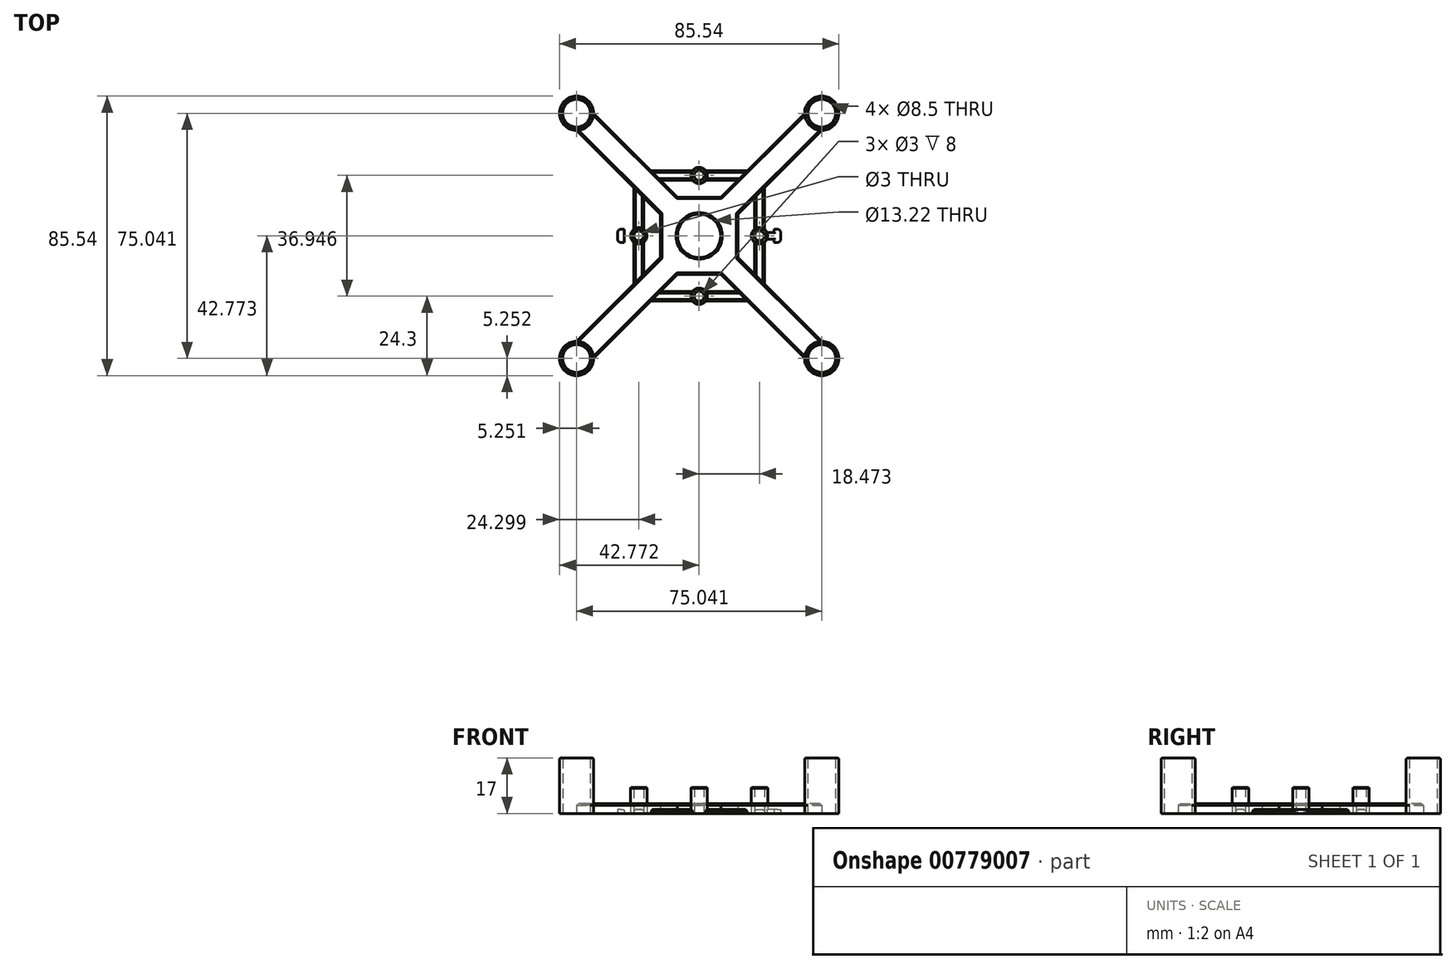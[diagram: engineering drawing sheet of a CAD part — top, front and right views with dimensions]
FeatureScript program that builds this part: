
annotation { "Feature Type Name" : "Feature", "Feature Type Description" : "" }
export const myFeature = defineFeature(function(context is Context, id is Id, definition is map)
    precondition{}
    {
        {
            var Q0;
            Q0=qCreatedBy(makeId("Top.planeOp"),FACE);
            var sketch = newSketch(context, id + "F0", { "sketchPlane" : qUnion([Q0])});
            skCircle(sketch, "E0", {"center": v(-48.89, -12.36) * mm, "radius": 4.25 * mm});
            skCircle(sketch, "E1", {"center": v(26.15, -12.36) * mm, "radius": 4.25 * mm});
            skCircle(sketch, "E2", {"center": v(26.15, 62.68) * mm, "radius": 4.25 * mm});
            skCircle(sketch, "E3", {"center": v(-48.89, 62.68) * mm, "radius": 4.25 * mm});
            skCircle(sketch, "E4", {"center": v(-48.89, 62.68) * mm, "radius": 5.25 * mm});
            skCircle(sketch, "E5", {"center": v(26.15, 62.68) * mm, "radius": 5.25 * mm});
            skCircle(sketch, "E6", {"center": v(26.15, -12.36) * mm, "radius": 5.25 * mm});
            skCircle(sketch, "E7", {"center": v(-48.89, -12.36) * mm, "radius": 5.25 * mm});
            skLineSegment(sketch, "E8", {"start": v(-43.64, -12.36) * mm, "end": v(-17.98, 13.3) * mm});
            skLineSegment(sketch, "E9", {"start": v(-48.89, -7.1) * mm, "end": v(-23.23, 18.55) * mm});
            skLineSegment(sketch, "E10", {"start": v(20.9, -12.36) * mm, "end": v(-4.76, 13.3) * mm});
            skLineSegment(sketch, "E11", {"start": v(26.15, -7.1) * mm, "end": v(0.5, 18.55) * mm});
            skLineSegment(sketch, "E12", {"start": v(20.9, 62.68) * mm, "end": v(-4.76, 37.02) * mm});
            skLineSegment(sketch, "E13", {"start": v(26.15, 57.43) * mm, "end": v(0.5, 31.77) * mm});
            skLineSegment(sketch, "E14", {"start": v(-43.64, 62.68) * mm, "end": v(-17.98, 37.02) * mm});
            skLineSegment(sketch, "E15", {"start": v(-48.89, 57.43) * mm, "end": v(-23.23, 31.77) * mm});
            skCircle(sketch, "E16", {"center": v(7.1, 25.16) * mm, "radius": 1.5 * mm});
            skCircle(sketch, "E17", {"center": v(-11.37, 43.64) * mm, "radius": 1.5 * mm});
            skCircle(sketch, "E18", {"center": v(-29.84, 25.16) * mm, "radius": 1.5 * mm});
            skCircle(sketch, "E19", {"center": v(-11.37, 6.69) * mm, "radius": 1.5 * mm});
            skCircle(sketch, "E20", {"center": v(-29.84, 25.16) * mm, "radius": 2.5 * mm});
            skCircle(sketch, "E21", {"center": v(-11.37, 43.64) * mm, "radius": 2.5 * mm});
            skCircle(sketch, "E22", {"center": v(7.1, 25.16) * mm, "radius": 2.5 * mm});
            skCircle(sketch, "E23", {"center": v(-11.37, 6.69) * mm, "radius": 2.5 * mm});
            skLineSegment(sketch, "E24", {"start": v(-36.34, 25.16) * mm, "end": v(-36.34, 27.16) * mm});
            skLineSegment(sketch, "E25", {"start": v(-36.34, 27.16) * mm, "end": v(-34.34, 27.16) * mm});
            skLineSegment(sketch, "E26", {"start": v(-34.34, 27.16) * mm, "end": v(-34.34, 23.16) * mm});
            skLineSegment(sketch, "E27", {"start": v(-34.34, 23.16) * mm, "end": v(-36.34, 23.16) * mm});
            skLineSegment(sketch, "E28", {"start": v(-36.34, 23.16) * mm, "end": v(-36.34, 25.16) * mm});
            skPoint(sketch, "E29.firstSnap0", {"position": v(-36.34, 26.16) * mm});
            skPoint(sketch, "E29.oppositeSnap0", {"position": v(-36.34, 24.16) * mm});
            skLineSegment(sketch, "E29.left", {"start": v(-34.34, 26.16) * mm, "end": v(-34.34, 24.16) * mm});
            skLineSegment(sketch, "E30", {"start": v(13.6, 25.16) * mm, "end": v(13.6, 27.16) * mm});
            skLineSegment(sketch, "E31", {"start": v(13.6, 27.16) * mm, "end": v(11.6, 27.16) * mm});
            skLineSegment(sketch, "E32", {"start": v(11.6, 27.16) * mm, "end": v(11.6, 23.16) * mm});
            skLineSegment(sketch, "E33", {"start": v(11.6, 23.16) * mm, "end": v(13.6, 23.16) * mm});
            skLineSegment(sketch, "E34", {"start": v(13.6, 23.16) * mm, "end": v(13.6, 25.16) * mm});
            skPoint(sketch, "E35.startSnap0", {"position": v(13.6, 26.16) * mm});
            skLineSegment(sketch, "E36", {"start": v(-34.34, 24.16) * mm, "end": v(-32.13, 24.16) * mm});
            skLineSegment(sketch, "E37", {"start": v(-34.34, 26.16) * mm, "end": v(-32.13, 26.16) * mm});
            skLineSegment(sketch, "E38", {"start": v(11.6, 24.16) * mm, "end": v(9.4, 24.16) * mm});
            skLineSegment(sketch, "E39", {"start": v(11.6, 26.16) * mm, "end": v(9.4, 26.16) * mm});
            skLineSegment(sketch, "E40", {"start": v(-23.23, 31.77) * mm, "end": v(-23.23, 18.55) * mm});
            skLineSegment(sketch, "E41", {"start": v(-17.98, 13.3) * mm, "end": v(-4.76, 13.3) * mm});
            skLineSegment(sketch, "E42", {"start": v(0.5, 18.55) * mm, "end": v(0.5, 31.77) * mm});
            skLineSegment(sketch, "E43", {"start": v(-4.76, 37.02) * mm, "end": v(-17.98, 37.02) * mm});
            skLineSegment(sketch, "E44", {"start": v(-28.34, 25.16) * mm, "end": v(-28.34, 36.89) * mm});
            skLineSegment(sketch, "E45", {"start": v(-28.34, 25.16) * mm, "end": v(-28.34, 13.44) * mm});
            skLineSegment(sketch, "E46", {"start": v(-31.34, 25.16) * mm, "end": v(-31.34, 39.89) * mm});
            skLineSegment(sketch, "E47", {"start": v(-31.34, 25.16) * mm, "end": v(-31.34, 10.44) * mm});
            skLineSegment(sketch, "E48", {"start": v(-11.37, 8.19) * mm, "end": v(-23.1, 8.19) * mm});
            skLineSegment(sketch, "E49", {"start": v(-11.37, 8.19) * mm, "end": v(0.35, 8.19) * mm});
            skLineSegment(sketch, "E50", {"start": v(-11.37, 5.19) * mm, "end": v(3.35, 5.19) * mm});
            skLineSegment(sketch, "E51", {"start": v(-11.37, 5.19) * mm, "end": v(-26.1, 5.19) * mm});
            skLineSegment(sketch, "E52", {"start": v(5.6, 25.16) * mm, "end": v(5.6, 13.44) * mm});
            skLineSegment(sketch, "E53", {"start": v(5.6, 25.16) * mm, "end": v(5.6, 36.89) * mm});
            skLineSegment(sketch, "E54", {"start": v(8.6, 25.16) * mm, "end": v(8.6, 39.89) * mm});
            skLineSegment(sketch, "E55", {"start": v(8.6, 25.16) * mm, "end": v(8.6, 10.44) * mm});
            skLineSegment(sketch, "E56", {"start": v(-11.37, 45.14) * mm, "end": v(3.35, 45.14) * mm});
            skLineSegment(sketch, "E57", {"start": v(-11.37, 45.14) * mm, "end": v(-26.1, 45.14) * mm});
            skLineSegment(sketch, "E58", {"start": v(-11.37, 42.14) * mm, "end": v(0.35, 42.14) * mm});
            skLineSegment(sketch, "E59", {"start": v(-11.37, 42.14) * mm, "end": v(-23.1, 42.14) * mm});
            skCircle(sketch, "E60", {"center": v(-11.37, 25.16) * mm, "radius": 6.61 * mm});
            skSolve(sketch);
        }
        {
            var Q0;
            {var subQ0=sQuery(id+"F0.wireOp",EDGE,"E45");var subQ1=sQuery(id+"F0.wireOp",EDGE,"E9");var subQ2=makeQuery(id+"F0.imprint","INTERSECT",VERTEX,{"derivedFrom":[subQ1,subQ0]});Q0=makeQuery(id+"F0.imprint","IMPRINT",FACE,{"disambiguationData":[TD([[makeQuery(id+"F0.imprint","IMPRINT",EDGE,{"disambiguationData":[TD([[subQ2,1.0]])],"derivedFrom":subQ1}),1.0]])]});}
            var Q1;
            {var subQ0=sQuery(id+"F0.wireOp",EDGE,"E56");var subQ1=sQuery(id+"F0.wireOp",EDGE,"E12");var subQ2=makeQuery(id+"F0.imprint","INTERSECT",VERTEX,{"derivedFrom":[subQ1,subQ0]});Q1=makeQuery(id+"F0.imprint","IMPRINT",FACE,{"disambiguationData":[TD([[makeQuery(id+"F0.imprint","IMPRINT",EDGE,{"disambiguationData":[TD([[subQ2,-1.0]])],"derivedFrom":subQ1}),-1.0]])]});}
            var Q2;
            {var subQ0=sQuery(id+"F0.wireOp",EDGE,"E57");var subQ1=sQuery(id+"F0.wireOp",EDGE,"E14");var subQ2=makeQuery(id+"F0.imprint","INTERSECT",VERTEX,{"derivedFrom":[subQ1,subQ0]});Q2=makeQuery(id+"F0.imprint","IMPRINT",FACE,{"disambiguationData":[TD([[makeQuery(id+"F0.imprint","IMPRINT",EDGE,{"disambiguationData":[TD([[subQ2,-1.0]])],"derivedFrom":subQ1}),1.0]])]});}
            var Q3;
            {var subQ21=sQuery(id+"F0.wireOp",EDGE,"E40");Q3=makeQuery(id+"F0.imprint","IMPRINT",FACE,{"disambiguationData":[TD([[makeQuery(id+"F0.imprint","IMPRINT",EDGE,{"derivedFrom":subQ21}),1.0]])]});}
            var Q4;
            {var subQ0=sQuery(id+"F0.wireOp",EDGE,"E49");var subQ1=sQuery(id+"F0.wireOp",EDGE,"E10");var subQ2=makeQuery(id+"F0.imprint","INTERSECT",VERTEX,{"derivedFrom":[subQ1,subQ0]});Q4=makeQuery(id+"F0.imprint","IMPRINT",FACE,{"disambiguationData":[TD([[makeQuery(id+"F0.imprint","IMPRINT",EDGE,{"disambiguationData":[TD([[subQ2,1.0]])],"derivedFrom":subQ1}),1.0]])]});}
            var Q5;
            {var subQ0=sQuery(id+"F0.wireOp",EDGE,"E52");var subQ1=sQuery(id+"F0.wireOp",EDGE,"E11");var subQ2=makeQuery(id+"F0.imprint","INTERSECT",VERTEX,{"derivedFrom":[subQ1,subQ0]});Q5=makeQuery(id+"F0.imprint","IMPRINT",FACE,{"disambiguationData":[TD([[makeQuery(id+"F0.imprint","IMPRINT",EDGE,{"disambiguationData":[TD([[subQ2,1.0]])],"derivedFrom":subQ1}),-1.0]])]});}
            var Q6;
            {var subQ0=sQuery(id+"F0.wireOp",EDGE,"E48");var subQ1=sQuery(id+"F0.wireOp",EDGE,"E8");var subQ2=makeQuery(id+"F0.imprint","INTERSECT",VERTEX,{"derivedFrom":[subQ1,subQ0]});Q6=makeQuery(id+"F0.imprint","IMPRINT",FACE,{"disambiguationData":[TD([[makeQuery(id+"F0.imprint","IMPRINT",EDGE,{"disambiguationData":[TD([[subQ2,1.0]])],"derivedFrom":subQ1}),-1.0]])]});}
            var Q7;
            {var subQ0=sQuery(id+"F0.wireOp",EDGE,"E44");var subQ1=sQuery(id+"F0.wireOp",EDGE,"E15");var subQ2=makeQuery(id+"F0.imprint","INTERSECT",VERTEX,{"derivedFrom":[subQ1,subQ0]});Q7=makeQuery(id+"F0.imprint","IMPRINT",FACE,{"disambiguationData":[TD([[makeQuery(id+"F0.imprint","IMPRINT",EDGE,{"disambiguationData":[TD([[subQ2,1.0]])],"derivedFrom":subQ1}),-1.0]])]});}
            var Q8;
            {var subQ0=sQuery(id+"F0.wireOp",EDGE,"E53");var subQ1=sQuery(id+"F0.wireOp",EDGE,"E13");var subQ2=makeQuery(id+"F0.imprint","INTERSECT",VERTEX,{"derivedFrom":[subQ1,subQ0]});Q8=makeQuery(id+"F0.imprint","IMPRINT",FACE,{"disambiguationData":[TD([[makeQuery(id+"F0.imprint","IMPRINT",EDGE,{"disambiguationData":[TD([[subQ2,1.0]])],"derivedFrom":subQ1}),1.0]])]});}
            var Q9;
            Q9=makeQuery(id+"F0.imprint","IMPRINT",FACE,{"disambiguationData":[TD([[makeQuery(id+"F0.imprint","IMPRINT",EDGE,{"derivedFrom":sQuery(id+"F0.wireOp",EDGE,"E1")}),-1.0]])]});
            var Q10;
            Q10=makeQuery(id+"F0.imprint","IMPRINT",FACE,{"disambiguationData":[TD([[makeQuery(id+"F0.imprint","IMPRINT",EDGE,{"derivedFrom":sQuery(id+"F0.wireOp",EDGE,"E0")}),-1.0]])]});
            var Q11;
            Q11=makeQuery(id+"F0.imprint","IMPRINT",FACE,{"disambiguationData":[TD([[makeQuery(id+"F0.imprint","IMPRINT",EDGE,{"derivedFrom":sQuery(id+"F0.wireOp",EDGE,"E3")}),-1.0]])]});
            var Q12;
            Q12=makeQuery(id+"F0.imprint","IMPRINT",FACE,{"disambiguationData":[TD([[makeQuery(id+"F0.imprint","IMPRINT",EDGE,{"derivedFrom":sQuery(id+"F0.wireOp",EDGE,"E2")}),-1.0]])]});
            var Q13;
            {var subQ0=sQuery(id+"F0.wireOp",EDGE,"E51");var subQ1=sQuery(id+"F0.wireOp",EDGE,"E23");var subQ2=makeQuery(id+"F0.imprint","INTERSECT",VERTEX,{"derivedFrom":[subQ1,subQ0]});Q13=makeQuery(id+"F0.imprint","IMPRINT",FACE,{"disambiguationData":[TD([[makeQuery(id+"F0.imprint","IMPRINT",EDGE,{"disambiguationData":[TD([[subQ2,-1.0]])],"derivedFrom":subQ1}),1.0]])]});}
            var Q14;
            {var subQ3=sQuery(id+"F0.wireOp",EDGE,"E50");var subQ5=sQuery(id+"F0.wireOp",EDGE,"E23");var subQ6=makeQuery(id+"F0.imprint","INTERSECT",VERTEX,{"derivedFrom":[subQ5,subQ3]});Q14=makeQuery(id+"F0.imprint","IMPRINT",FACE,{"disambiguationData":[TD([[makeQuery(id+"F0.imprint","IMPRINT",EDGE,{"disambiguationData":[TD([[subQ6,-1.0]])],"derivedFrom":subQ5}),1.0]])]});}
            var Q15;
            {var subQ0=sQuery(id+"F0.wireOp",EDGE,"E59");var subQ1=sQuery(id+"F0.wireOp",EDGE,"E21");var subQ2=makeQuery(id+"F0.imprint","INTERSECT",VERTEX,{"derivedFrom":[subQ1,subQ0]});Q15=makeQuery(id+"F0.imprint","IMPRINT",FACE,{"disambiguationData":[TD([[makeQuery(id+"F0.imprint","IMPRINT",EDGE,{"disambiguationData":[TD([[subQ2,-1.0]])],"derivedFrom":subQ1}),1.0]])]});}
            var Q16;
            {var subQ3=sQuery(id+"F0.wireOp",EDGE,"E51");var subQ5=sQuery(id+"F0.wireOp",EDGE,"E23");var subQ6=makeQuery(id+"F0.imprint","INTERSECT",VERTEX,{"derivedFrom":[subQ5,subQ3]});Q16=makeQuery(id+"F0.imprint","IMPRINT",FACE,{"disambiguationData":[TD([[makeQuery(id+"F0.imprint","IMPRINT",EDGE,{"disambiguationData":[TD([[subQ6,1.0]])],"derivedFrom":subQ5}),1.0]])]});}
            var Q17;
            {var subQ0=sQuery(id+"F0.wireOp",EDGE,"E44");var subQ1=sQuery(id+"F0.wireOp",EDGE,"E20");var subQ2=makeQuery(id+"F0.imprint","INTERSECT",VERTEX,{"derivedFrom":[subQ1,subQ0]});Q17=makeQuery(id+"F0.imprint","IMPRINT",FACE,{"disambiguationData":[TD([[makeQuery(id+"F0.imprint","IMPRINT",EDGE,{"disambiguationData":[TD([[subQ2,1.0]])],"derivedFrom":subQ1}),1.0]])]});}
            var Q18;
            {var subQ0=sQuery(id+"F0.wireOp",EDGE,"E57");var subQ5=sQuery(id+"F0.wireOp",EDGE,"E21");var subQ6=makeQuery(id+"F0.imprint","INTERSECT",VERTEX,{"derivedFrom":[subQ5,subQ0]});Q18=makeQuery(id+"F0.imprint","IMPRINT",FACE,{"disambiguationData":[TD([[makeQuery(id+"F0.imprint","IMPRINT",EDGE,{"disambiguationData":[TD([[subQ6,-1.0]])],"derivedFrom":subQ5}),1.0]])]});}
            var Q19;
            {var subQ0=sQuery(id+"F0.wireOp",EDGE,"E57");var subQ1=sQuery(id+"F0.wireOp",EDGE,"E21");var subQ2=makeQuery(id+"F0.imprint","INTERSECT",VERTEX,{"derivedFrom":[subQ1,subQ0]});Q19=makeQuery(id+"F0.imprint","IMPRINT",FACE,{"disambiguationData":[TD([[makeQuery(id+"F0.imprint","IMPRINT",EDGE,{"disambiguationData":[TD([[subQ2,1.0]])],"derivedFrom":subQ1}),1.0]])]});}
            var Q20;
            {var subQ3=sQuery(id+"F0.wireOp",EDGE,"E46");var subQ5=sQuery(id+"F0.wireOp",EDGE,"E20");var subQ6=makeQuery(id+"F0.imprint","INTERSECT",VERTEX,{"derivedFrom":[subQ5,subQ3]});Q20=makeQuery(id+"F0.imprint","IMPRINT",FACE,{"disambiguationData":[TD([[makeQuery(id+"F0.imprint","IMPRINT",EDGE,{"disambiguationData":[TD([[subQ6,1.0]])],"derivedFrom":subQ5}),1.0]])]});}
            var Q21;
            {var subQ0=sQuery(id+"F0.wireOp",EDGE,"E48");var subQ1=sQuery(id+"F0.wireOp",EDGE,"E23");var subQ2=makeQuery(id+"F0.imprint","INTERSECT",VERTEX,{"derivedFrom":[subQ1,subQ0]});Q21=makeQuery(id+"F0.imprint","IMPRINT",FACE,{"disambiguationData":[TD([[makeQuery(id+"F0.imprint","IMPRINT",EDGE,{"disambiguationData":[TD([[subQ2,1.0]])],"derivedFrom":subQ1}),1.0]])]});}
            var Q22;
            {var subQ0=sQuery(id+"F0.wireOp",EDGE,"E56");var subQ5=sQuery(id+"F0.wireOp",EDGE,"E21");var subQ7=makeQuery(id+"F0.imprint","INTERSECT",VERTEX,{"derivedFrom":[subQ5,subQ0]});Q22=makeQuery(id+"F0.imprint","IMPRINT",FACE,{"disambiguationData":[TD([[makeQuery(id+"F0.imprint","IMPRINT",EDGE,{"disambiguationData":[TD([[subQ7,1.0]])],"derivedFrom":subQ5}),1.0]])]});}
            var Q23;
            Q23=makeQuery(id+"F0.imprint","IMPRINT",FACE,{"disambiguationData":[TD([[makeQuery(id+"F0.imprint","IMPRINT",EDGE,{"derivedFrom":sQuery(id+"F0.wireOp",EDGE,"E30")}),1.0]])]});
            var Q24;
            {var subQ3=sQuery(id+"F0.wireOp",EDGE,"E55");var subQ5=sQuery(id+"F0.wireOp",EDGE,"E22");var subQ6=makeQuery(id+"F0.imprint","INTERSECT",VERTEX,{"derivedFrom":[subQ5,subQ3]});Q24=makeQuery(id+"F0.imprint","IMPRINT",FACE,{"disambiguationData":[TD([[makeQuery(id+"F0.imprint","IMPRINT",EDGE,{"disambiguationData":[TD([[subQ6,1.0]])],"derivedFrom":subQ5}),1.0]])]});}
            var Q25;
            {var subQ0=sQuery(id+"F0.wireOp",EDGE,"E53");var subQ1=sQuery(id+"F0.wireOp",EDGE,"E22");var subQ2=makeQuery(id+"F0.imprint","INTERSECT",VERTEX,{"derivedFrom":[subQ1,subQ0]});Q25=makeQuery(id+"F0.imprint","IMPRINT",FACE,{"disambiguationData":[TD([[makeQuery(id+"F0.imprint","IMPRINT",EDGE,{"disambiguationData":[TD([[subQ2,-1.0]])],"derivedFrom":subQ1}),1.0]])]});}
            var Q26;
            {var subQ3=sQuery(id+"F0.wireOp",EDGE,"E54");var subQ5=sQuery(id+"F0.wireOp",EDGE,"E22");var subQ6=makeQuery(id+"F0.imprint","INTERSECT",VERTEX,{"derivedFrom":[subQ5,subQ3]});Q26=makeQuery(id+"F0.imprint","IMPRINT",FACE,{"disambiguationData":[TD([[makeQuery(id+"F0.imprint","IMPRINT",EDGE,{"disambiguationData":[TD([[subQ6,-1.0]])],"derivedFrom":subQ5}),1.0]])]});}
            var Q27;
            {var subQ0=sQuery(id+"F0.wireOp",EDGE,"E38");Q27=makeQuery(id+"F0.imprint","IMPRINT",FACE,{"disambiguationData":[TD([[makeQuery(id+"F0.imprint","IMPRINT",EDGE,{"derivedFrom":subQ0}),-1.0]])]});}
            var Q28;
            {var subQ3=sQuery(id+"F0.wireOp",EDGE,"E47");var subQ5=sQuery(id+"F0.wireOp",EDGE,"E20");var subQ6=makeQuery(id+"F0.imprint","INTERSECT",VERTEX,{"derivedFrom":[subQ5,subQ3]});Q28=makeQuery(id+"F0.imprint","IMPRINT",FACE,{"disambiguationData":[TD([[makeQuery(id+"F0.imprint","IMPRINT",EDGE,{"disambiguationData":[TD([[subQ6,-1.0]])],"derivedFrom":subQ5}),1.0]])]});}
            var Q29;
            Q29=makeQuery(id+"F0.imprint","IMPRINT",FACE,{"disambiguationData":[TD([[makeQuery(id+"F0.imprint","IMPRINT",EDGE,{"derivedFrom":sQuery(id+"F0.wireOp",EDGE,"E29.left")}),1.0]])]});
            var Q30;
            {var subQ3=sQuery(id+"F0.wireOp",EDGE,"E22");var subQ7=makeQuery(id+"F0.imprint","INTERSECT",VERTEX,{"derivedFrom":[subQ3,sQuery(id+"F0.wireOp",EDGE,"E39")]});Q30=makeQuery(id+"F0.imprint","IMPRINT",FACE,{"disambiguationData":[TD([[makeQuery(id+"F0.imprint","IMPRINT",EDGE,{"disambiguationData":[TD([[subQ7,-1.0]])],"derivedFrom":subQ3}),1.0]])]});}
            var Q31;
            Q31=makeQuery(id+"F0.imprint","IMPRINT",FACE,{"disambiguationData":[TD([[makeQuery(id+"F0.imprint","IMPRINT",EDGE,{"derivedFrom":sQuery(id+"F0.wireOp",EDGE,"E24")}),-1.0]])]});
            var Q32;
            {var subQ0=sQuery(id+"F0.wireOp",EDGE,"E20");var subQ4=makeQuery(id+"F0.imprint","INTERSECT",VERTEX,{"derivedFrom":[subQ0,sQuery(id+"F0.wireOp",EDGE,"E37")]});Q32=makeQuery(id+"F0.imprint","IMPRINT",FACE,{"disambiguationData":[TD([[makeQuery(id+"F0.imprint","IMPRINT",EDGE,{"disambiguationData":[TD([[subQ4,1.0]])],"derivedFrom":subQ0}),1.0]])]});}
            var Q33;
            {var subQ0=sQuery(id+"F0.wireOp",EDGE,"EpfRIm18-ZJDy-jQLn-HDGs-4fdOUsAAegEl");Q33=makeQuery(id+"F0.imprint","IMPRINT",FACE,{"disambiguationData":[TD([[makeQuery(id+"F0.imprint","IMPRINT",EDGE,{"derivedFrom":subQ0}),1.0]])]});}
            var Q34;
            {var subQ2=sQuery(id+"F0.wireOp",EDGE,"o9JcbMGx-JBcp-YJli-rHgj-RiYyzjxsNXtp");Q34=makeQuery(id+"F0.imprint","IMPRINT",FACE,{"disambiguationData":[TD([[makeQuery(id+"F0.imprint","IMPRINT",EDGE,{"derivedFrom":subQ2}),1.0]])]});}
            var Q35;
            {var subQ0=sQuery(id+"F0.wireOp",EDGE,"NZc1Y8mV-QyNj-f26t-cdzd-yLMniGNX0fs4");Q35=makeQuery(id+"F0.imprint","IMPRINT",FACE,{"disambiguationData":[TD([[makeQuery(id+"F0.imprint","IMPRINT",EDGE,{"derivedFrom":subQ0}),-1.0]])]});}
            var Q36;
            {var subQ2=sQuery(id+"F0.wireOp",EDGE,"Yo5fGIDt-ger0-HmA0-dRW6-T6dsiI5SlUzT");Q36=makeQuery(id+"F0.imprint","IMPRINT",FACE,{"disambiguationData":[TD([[makeQuery(id+"F0.imprint","IMPRINT",EDGE,{"derivedFrom":subQ2}),1.0]])]});}
            extrude(context, id + "F1", {"entities" : qUnion([Q0, Q1, Q2, Q3, Q4, Q5, Q6, Q7, Q8, Q9, Q10, Q11, Q12, Q13, Q14, Q15, Q16, Q17, Q18, Q19, Q20, Q21, Q22, Q23, Q24, Q25, Q26, Q27, Q28, Q29, Q30, Q31, Q32, Q33, Q34, Q35, Q36]), "depth" : 1.2 * mm, "offsetDistance" : 25 * mm});
        }
        {
            var Q0;
            Q0=makeQuery(id+"F0.imprint","IMPRINT",FACE,{"disambiguationData":[TD([[makeQuery(id+"F0.imprint","IMPRINT",EDGE,{"derivedFrom":sQuery(id+"F0.wireOp",EDGE,"E0")}),-1.0]])]});
            var Q1;
            Q1=makeQuery(id+"F0.imprint","IMPRINT",FACE,{"disambiguationData":[TD([[makeQuery(id+"F0.imprint","IMPRINT",EDGE,{"derivedFrom":sQuery(id+"F0.wireOp",EDGE,"E3")}),-1.0]])]});
            var Q2;
            Q2=makeQuery(id+"F0.imprint","IMPRINT",FACE,{"disambiguationData":[TD([[makeQuery(id+"F0.imprint","IMPRINT",EDGE,{"derivedFrom":sQuery(id+"F0.wireOp",EDGE,"E2")}),-1.0]])]});
            var Q3;
            Q3=makeQuery(id+"F0.imprint","IMPRINT",FACE,{"disambiguationData":[TD([[makeQuery(id+"F0.imprint","IMPRINT",EDGE,{"derivedFrom":sQuery(id+"F0.wireOp",EDGE,"E1")}),-1.0]])]});
            extrude(context, id + "F2", {"entities" : qUnion([Q0, Q1, Q2, Q3]), "operationType" : NewBodyOperationType.ADD, "depth" : 17 * mm, "offsetDistance" : 25 * mm});
        }
        {
            var Q0;
            {var subQ21=sQuery(id+"F0.wireOp",EDGE,"E40");Q0=makeQuery(id+"F0.imprint","IMPRINT",FACE,{"disambiguationData":[TD([[makeQuery(id+"F0.imprint","IMPRINT",EDGE,{"derivedFrom":subQ21}),1.0]])]});}
            extrude(context, id + "F3", {"entities" : qUnion([Q0]), "operationType" : NewBodyOperationType.ADD, "depth" : 3 * mm, "offsetDistance" : 25 * mm});
        }
        {
            var Q0;
            Q0=makeQuery(id+"F2.opExtrude","CAP_EDGE",EDGE,{"disambiguationData":[OSD([sQuery(id+"F0.wireOp",EDGE,"E6")])],"isStart":false});
            var Q1;
            Q1=makeQuery(id+"F2.opExtrude","CAP_EDGE",EDGE,{"disambiguationData":[OSD([sQuery(id+"F0.wireOp",EDGE,"E5")])],"isStart":false});
            var Q2;
            Q2=makeQuery(id+"F2.opExtrude","CAP_EDGE",EDGE,{"disambiguationData":[OSD([sQuery(id+"F0.wireOp",EDGE,"E7")])],"isStart":false});
            var Q3;
            Q3=makeQuery(id+"F2.opExtrude","CAP_EDGE",EDGE,{"disambiguationData":[OSD([sQuery(id+"F0.wireOp",EDGE,"E4")])],"isStart":false});
            fillet(context, id + "F4", {"entities" : qUnion([Q0, Q1, Q2, Q3]), "radius" : 0.5 * mm, "tangentPropagation" : true, "allowEdgeOverflow" : false});
        }
        {
            var Q0;
            {var subQ1=sQuery(id+"F0.wireOp",EDGE,"E22");var subQ9=sQuery(id+"F0.wireOp",EDGE,"XLftUaR9-tIFC-lNXf-Dolu-BYzKN6O2kL2o.top");var subQ11=makeQuery(id+"F0.imprint","INTERSECT",VERTEX,{"derivedFrom":[subQ9,subQ1]});Q0=makeQuery(id+"F0.imprint","IMPRINT",FACE,{"disambiguationData":[TD([[makeQuery(id+"F0.imprint","IMPRINT",EDGE,{"disambiguationData":[TD([[subQ11,-1.0]])],"derivedFrom":subQ9}),-1.0]])]});}
            var Q1;
            {var subQ0=sQuery(id+"F0.wireOp",EDGE,"E22");var subQ1=sQuery(id+"F0.wireOp",EDGE,"XLftUaR9-tIFC-lNXf-Dolu-BYzKN6O2kL2o.top");var subQ2=makeQuery(id+"F0.imprint","INTERSECT",VERTEX,{"derivedFrom":[subQ1,subQ0]});Q1=makeQuery(id+"F0.imprint","IMPRINT",FACE,{"disambiguationData":[TD([[makeQuery(id+"F0.imprint","IMPRINT",EDGE,{"disambiguationData":[TD([[subQ2,-1.0]])],"derivedFrom":subQ1}),1.0]])]});}
            var Q2;
            {var subQ0=sQuery(id+"F0.wireOp",EDGE,"E21");var subQ4=sQuery(id+"F0.wireOp",EDGE,"XLftUaR9-tIFC-lNXf-Dolu-BYzKN6O2kL2o.bottom");var subQ8=makeQuery(id+"F0.imprint","INTERSECT",VERTEX,{"derivedFrom":[subQ4,subQ0]});Q2=makeQuery(id+"F0.imprint","IMPRINT",FACE,{"disambiguationData":[TD([[makeQuery(id+"F0.imprint","IMPRINT",EDGE,{"disambiguationData":[TD([[subQ8,-1.0]])],"derivedFrom":subQ4}),1.0]])]});}
            var Q3;
            {var subQ0=sQuery(id+"F0.wireOp",EDGE,"E21");var subQ1=sQuery(id+"F0.wireOp",EDGE,"XLftUaR9-tIFC-lNXf-Dolu-BYzKN6O2kL2o.bottom");var subQ2=makeQuery(id+"F0.imprint","INTERSECT",VERTEX,{"derivedFrom":[subQ1,subQ0]});Q3=makeQuery(id+"F0.imprint","IMPRINT",FACE,{"disambiguationData":[TD([[makeQuery(id+"F0.imprint","IMPRINT",EDGE,{"disambiguationData":[TD([[subQ2,-1.0]])],"derivedFrom":subQ1}),-1.0]])]});}
            var Q4;
            {var subQ3=sQuery(id+"F0.wireOp",EDGE,"XLftUaR9-tIFC-lNXf-Dolu-BYzKN6O2kL2o.bottom");var subQ5=sQuery(id+"F0.wireOp",EDGE,"E18");var subQ6=makeQuery(id+"F0.imprint","INTERSECT",VERTEX,{"derivedFrom":[subQ3,subQ5]});Q4=makeQuery(id+"F0.imprint","IMPRINT",FACE,{"disambiguationData":[TD([[makeQuery(id+"F0.imprint","IMPRINT",EDGE,{"disambiguationData":[TD([[subQ6,-1.0]])],"derivedFrom":subQ3}),1.0]])]});}
            var Q5;
            {var subQ0=sQuery(id+"F0.wireOp",EDGE,"E18");var subQ1=sQuery(id+"F0.wireOp",EDGE,"XLftUaR9-tIFC-lNXf-Dolu-BYzKN6O2kL2o.bottom");var subQ2=makeQuery(id+"F0.imprint","INTERSECT",VERTEX,{"derivedFrom":[subQ1,subQ0]});Q5=makeQuery(id+"F0.imprint","IMPRINT",FACE,{"disambiguationData":[TD([[makeQuery(id+"F0.imprint","IMPRINT",EDGE,{"disambiguationData":[TD([[subQ2,-1.0]])],"derivedFrom":subQ1}),-1.0]])]});}
            var Q6;
            {var subQ5=sQuery(id+"F0.wireOp",EDGE,"E19");var subQ7=sQuery(id+"F0.wireOp",EDGE,"XLftUaR9-tIFC-lNXf-Dolu-BYzKN6O2kL2o.top");var subQ8=makeQuery(id+"F0.imprint","INTERSECT",VERTEX,{"derivedFrom":[subQ7,subQ5]});Q6=makeQuery(id+"F0.imprint","IMPRINT",FACE,{"disambiguationData":[TD([[makeQuery(id+"F0.imprint","IMPRINT",EDGE,{"disambiguationData":[TD([[subQ8,-1.0]])],"derivedFrom":subQ7}),-1.0]])]});}
            var Q7;
            {var subQ0=sQuery(id+"F0.wireOp",EDGE,"E19");var subQ1=sQuery(id+"F0.wireOp",EDGE,"XLftUaR9-tIFC-lNXf-Dolu-BYzKN6O2kL2o.top");var subQ2=makeQuery(id+"F0.imprint","INTERSECT",VERTEX,{"derivedFrom":[subQ1,subQ0]});Q7=makeQuery(id+"F0.imprint","IMPRINT",FACE,{"disambiguationData":[TD([[makeQuery(id+"F0.imprint","IMPRINT",EDGE,{"disambiguationData":[TD([[subQ2,-1.0]])],"derivedFrom":subQ1}),1.0]])]});}
            var Q8;
            {var subQ0=sQuery(id+"F0.wireOp",EDGE,"lyLyndLk-WEsC-TF12-UGhv-u17dHFd35aoe");var subQ1=sQuery(id+"F0.wireOp",EDGE,"E20");var subQ3=makeQuery(id+"F0.imprint","INTERSECT",VERTEX,{"derivedFrom":[subQ1,subQ0]});Q8=makeQuery(id+"F0.imprint","IMPRINT",FACE,{"disambiguationData":[TD([[makeQuery(id+"F0.imprint","IMPRINT",EDGE,{"disambiguationData":[TD([[subQ3,1.0]])],"derivedFrom":subQ1}),1.0]])]});}
            var Q9;
            {var subQ0=sQuery(id+"F0.wireOp",EDGE,"ntcdMGfk-Catd-EpIT-ZPEj-Ae9I5mEbvvME");var subQ1=sQuery(id+"F0.wireOp",EDGE,"E20");var subQ3=makeQuery(id+"F0.imprint","INTERSECT",VERTEX,{"derivedFrom":[subQ1,subQ0]});Q9=makeQuery(id+"F0.imprint","IMPRINT",FACE,{"disambiguationData":[TD([[makeQuery(id+"F0.imprint","IMPRINT",EDGE,{"disambiguationData":[TD([[subQ3,-1.0]])],"derivedFrom":subQ1}),1.0]])]});}
            var Q10;
            {var subQ0=sQuery(id+"F0.wireOp",EDGE,"xX9YZJYt-xaks-Jpnu-0jvK-vmhjYCmHct0m");var subQ1=sQuery(id+"F0.wireOp",EDGE,"E23");var subQ3=makeQuery(id+"F0.imprint","INTERSECT",VERTEX,{"derivedFrom":[subQ1,subQ0]});Q10=makeQuery(id+"F0.imprint","IMPRINT",FACE,{"disambiguationData":[TD([[makeQuery(id+"F0.imprint","IMPRINT",EDGE,{"disambiguationData":[TD([[subQ3,-1.0]])],"derivedFrom":subQ1}),1.0]])]});}
            var Q11;
            {var subQ0=sQuery(id+"F0.wireOp",EDGE,"WUkc14mb-6nAl-cFaL-uvs8-OnrZHplLQN3j");var subQ1=sQuery(id+"F0.wireOp",EDGE,"E23");var subQ3=makeQuery(id+"F0.imprint","INTERSECT",VERTEX,{"derivedFrom":[subQ1,subQ0]});Q11=makeQuery(id+"F0.imprint","IMPRINT",FACE,{"disambiguationData":[TD([[makeQuery(id+"F0.imprint","IMPRINT",EDGE,{"disambiguationData":[TD([[subQ3,1.0]])],"derivedFrom":subQ1}),1.0]])]});}
            var Q12;
            {var subQ0=sQuery(id+"F0.wireOp",EDGE,"Glc09Lzf-w6aO-Foie-pjly-yRbPWOaYHaXg");var subQ1=sQuery(id+"F0.wireOp",EDGE,"E22");var subQ3=makeQuery(id+"F0.imprint","INTERSECT",VERTEX,{"derivedFrom":[subQ1,subQ0]});Q12=makeQuery(id+"F0.imprint","IMPRINT",FACE,{"disambiguationData":[TD([[makeQuery(id+"F0.imprint","IMPRINT",EDGE,{"disambiguationData":[TD([[subQ3,1.0]])],"derivedFrom":subQ1}),1.0]])]});}
            var Q13;
            {var subQ0=sQuery(id+"F0.wireOp",EDGE,"8GtNXrsa-7Jlm-bfA7-YNFt-d0DOuLFm2n6T");var subQ1=sQuery(id+"F0.wireOp",EDGE,"E22");var subQ3=makeQuery(id+"F0.imprint","INTERSECT",VERTEX,{"derivedFrom":[subQ1,subQ0]});Q13=makeQuery(id+"F0.imprint","IMPRINT",FACE,{"disambiguationData":[TD([[makeQuery(id+"F0.imprint","IMPRINT",EDGE,{"disambiguationData":[TD([[subQ3,-1.0]])],"derivedFrom":subQ1}),1.0]])]});}
            var Q14;
            {var subQ0=sQuery(id+"F0.wireOp",EDGE,"U5ZoAzme-not6-6lWv-rdHy-XvJVbGq4S0oc");var subQ1=sQuery(id+"F0.wireOp",EDGE,"E21");var subQ3=makeQuery(id+"F0.imprint","INTERSECT",VERTEX,{"derivedFrom":[subQ1,subQ0]});Q14=makeQuery(id+"F0.imprint","IMPRINT",FACE,{"disambiguationData":[TD([[makeQuery(id+"F0.imprint","IMPRINT",EDGE,{"disambiguationData":[TD([[subQ3,1.0]])],"derivedFrom":subQ1}),1.0]])]});}
            var Q15;
            {var subQ0=sQuery(id+"F0.wireOp",EDGE,"qDDfUkpN-YX3d-6aV8-hpiR-mt3p9fcYLafk");var subQ1=sQuery(id+"F0.wireOp",EDGE,"E21");var subQ3=makeQuery(id+"F0.imprint","INTERSECT",VERTEX,{"derivedFrom":[subQ1,subQ0]});Q15=makeQuery(id+"F0.imprint","IMPRINT",FACE,{"disambiguationData":[TD([[makeQuery(id+"F0.imprint","IMPRINT",EDGE,{"disambiguationData":[TD([[subQ3,-1.0]])],"derivedFrom":subQ1}),1.0]])]});}
            var Q16;
            {var subQ0=sQuery(id+"F0.wireOp",EDGE,"E56");var subQ5=sQuery(id+"F0.wireOp",EDGE,"E21");var subQ7=makeQuery(id+"F0.imprint","INTERSECT",VERTEX,{"derivedFrom":[subQ5,subQ0]});Q16=makeQuery(id+"F0.imprint","IMPRINT",FACE,{"disambiguationData":[TD([[makeQuery(id+"F0.imprint","IMPRINT",EDGE,{"disambiguationData":[TD([[subQ7,1.0]])],"derivedFrom":subQ5}),1.0]])]});}
            var Q17;
            {var subQ0=sQuery(id+"F0.wireOp",EDGE,"E57");var subQ5=sQuery(id+"F0.wireOp",EDGE,"E21");var subQ6=makeQuery(id+"F0.imprint","INTERSECT",VERTEX,{"derivedFrom":[subQ5,subQ0]});Q17=makeQuery(id+"F0.imprint","IMPRINT",FACE,{"disambiguationData":[TD([[makeQuery(id+"F0.imprint","IMPRINT",EDGE,{"disambiguationData":[TD([[subQ6,-1.0]])],"derivedFrom":subQ5}),1.0]])]});}
            var Q18;
            {var subQ3=sQuery(id+"F0.wireOp",EDGE,"E47");var subQ5=sQuery(id+"F0.wireOp",EDGE,"E20");var subQ6=makeQuery(id+"F0.imprint","INTERSECT",VERTEX,{"derivedFrom":[subQ5,subQ3]});Q18=makeQuery(id+"F0.imprint","IMPRINT",FACE,{"disambiguationData":[TD([[makeQuery(id+"F0.imprint","IMPRINT",EDGE,{"disambiguationData":[TD([[subQ6,-1.0]])],"derivedFrom":subQ5}),1.0]])]});}
            var Q19;
            {var subQ3=sQuery(id+"F0.wireOp",EDGE,"E46");var subQ5=sQuery(id+"F0.wireOp",EDGE,"E20");var subQ6=makeQuery(id+"F0.imprint","INTERSECT",VERTEX,{"derivedFrom":[subQ5,subQ3]});Q19=makeQuery(id+"F0.imprint","IMPRINT",FACE,{"disambiguationData":[TD([[makeQuery(id+"F0.imprint","IMPRINT",EDGE,{"disambiguationData":[TD([[subQ6,1.0]])],"derivedFrom":subQ5}),1.0]])]});}
            var Q20;
            {var subQ0=sQuery(id+"F0.wireOp",EDGE,"E44");var subQ1=sQuery(id+"F0.wireOp",EDGE,"E20");var subQ2=makeQuery(id+"F0.imprint","INTERSECT",VERTEX,{"derivedFrom":[subQ1,subQ0]});Q20=makeQuery(id+"F0.imprint","IMPRINT",FACE,{"disambiguationData":[TD([[makeQuery(id+"F0.imprint","IMPRINT",EDGE,{"disambiguationData":[TD([[subQ2,1.0]])],"derivedFrom":subQ1}),1.0]])]});}
            var Q21;
            {var subQ3=sQuery(id+"F0.wireOp",EDGE,"E54");var subQ5=sQuery(id+"F0.wireOp",EDGE,"E22");var subQ6=makeQuery(id+"F0.imprint","INTERSECT",VERTEX,{"derivedFrom":[subQ5,subQ3]});Q21=makeQuery(id+"F0.imprint","IMPRINT",FACE,{"disambiguationData":[TD([[makeQuery(id+"F0.imprint","IMPRINT",EDGE,{"disambiguationData":[TD([[subQ6,-1.0]])],"derivedFrom":subQ5}),1.0]])]});}
            var Q22;
            {var subQ3=sQuery(id+"F0.wireOp",EDGE,"E55");var subQ5=sQuery(id+"F0.wireOp",EDGE,"E22");var subQ6=makeQuery(id+"F0.imprint","INTERSECT",VERTEX,{"derivedFrom":[subQ5,subQ3]});Q22=makeQuery(id+"F0.imprint","IMPRINT",FACE,{"disambiguationData":[TD([[makeQuery(id+"F0.imprint","IMPRINT",EDGE,{"disambiguationData":[TD([[subQ6,1.0]])],"derivedFrom":subQ5}),1.0]])]});}
            var Q23;
            {var subQ0=sQuery(id+"F0.wireOp",EDGE,"E53");var subQ1=sQuery(id+"F0.wireOp",EDGE,"E22");var subQ2=makeQuery(id+"F0.imprint","INTERSECT",VERTEX,{"derivedFrom":[subQ1,subQ0]});Q23=makeQuery(id+"F0.imprint","IMPRINT",FACE,{"disambiguationData":[TD([[makeQuery(id+"F0.imprint","IMPRINT",EDGE,{"disambiguationData":[TD([[subQ2,-1.0]])],"derivedFrom":subQ1}),1.0]])]});}
            var Q24;
            {var subQ3=sQuery(id+"F0.wireOp",EDGE,"E51");var subQ5=sQuery(id+"F0.wireOp",EDGE,"E23");var subQ6=makeQuery(id+"F0.imprint","INTERSECT",VERTEX,{"derivedFrom":[subQ5,subQ3]});Q24=makeQuery(id+"F0.imprint","IMPRINT",FACE,{"disambiguationData":[TD([[makeQuery(id+"F0.imprint","IMPRINT",EDGE,{"disambiguationData":[TD([[subQ6,1.0]])],"derivedFrom":subQ5}),1.0]])]});}
            var Q25;
            {var subQ3=sQuery(id+"F0.wireOp",EDGE,"E50");var subQ5=sQuery(id+"F0.wireOp",EDGE,"E23");var subQ6=makeQuery(id+"F0.imprint","INTERSECT",VERTEX,{"derivedFrom":[subQ5,subQ3]});Q25=makeQuery(id+"F0.imprint","IMPRINT",FACE,{"disambiguationData":[TD([[makeQuery(id+"F0.imprint","IMPRINT",EDGE,{"disambiguationData":[TD([[subQ6,-1.0]])],"derivedFrom":subQ5}),1.0]])]});}
            extrude(context, id + "F5", {"entities" : qUnion([Q0, Q1, Q2, Q3, Q4, Q5, Q6, Q7, Q8, Q9, Q10, Q11, Q12, Q13, Q14, Q15, Q16, Q17, Q18, Q19, Q20, Q21, Q22, Q23, Q24, Q25]), "operationType" : NewBodyOperationType.ADD, "depth" : 8 * mm, "offsetDistance" : 25 * mm});
        }
        {
            var Q0;
            Q0=makeQuery(id+"F1.opExtrude","SWEPT_EDGE",EDGE,{"disambiguationData":[OSD([sQuery(id+"F0.wireOp",EDGE,"E27"),sQuery(id+"F0.wireOp",EDGE,"E28")])]});
            var Q1;
            Q1=makeQuery(id+"F1.opExtrude","SWEPT_EDGE",EDGE,{"disambiguationData":[OSD([sQuery(id+"F0.wireOp",EDGE,"E24"),sQuery(id+"F0.wireOp",EDGE,"E25")])]});
            var Q2;
            Q2=makeQuery(id+"F1.opExtrude","SWEPT_EDGE",EDGE,{"disambiguationData":[OSD([sQuery(id+"F0.wireOp",EDGE,"E33"),sQuery(id+"F0.wireOp",EDGE,"E34")])]});
            var Q3;
            Q3=makeQuery(id+"F1.opExtrude","SWEPT_EDGE",EDGE,{"disambiguationData":[OSD([sQuery(id+"F0.wireOp",EDGE,"E30"),sQuery(id+"F0.wireOp",EDGE,"E31")])]});
            fillet(context, id + "F6", {"entities" : qUnion([Q0, Q1, Q2, Q3]), "radius" : 1 * mm, "tangentPropagation" : true, "allowEdgeOverflow" : false});
        }
        {
            var Q0;
            Q0=makeQuery(id+"F5.opExtrude","CAP_EDGE",EDGE,{"disambiguationData":[OSD([sQuery(id+"F0.wireOp",EDGE,"E20")])],"isStart":false});
            var Q1;
            Q1=makeQuery(id+"F5.opExtrude","CAP_EDGE",EDGE,{"disambiguationData":[OSD([sQuery(id+"F0.wireOp",EDGE,"E23")])],"isStart":false});
            var Q2;
            Q2=makeQuery(id+"F5.opExtrude","CAP_EDGE",EDGE,{"disambiguationData":[OSD([sQuery(id+"F0.wireOp",EDGE,"E22")])],"isStart":false});
            var Q3;
            Q3=makeQuery(id+"F5.opExtrude","CAP_EDGE",EDGE,{"disambiguationData":[OSD([sQuery(id+"F0.wireOp",EDGE,"E21")])],"isStart":false});
            var Q4;
            Q4=makeQuery(id+"F5.opExtrude","CAP_EDGE",EDGE,{"disambiguationData":[OSD([sQuery(id+"F0.wireOp",EDGE,"E18")])],"isStart":false});
            var Q5;
            Q5=makeQuery(id+"F2.opExtrude","CAP_EDGE",EDGE,{"disambiguationData":[OSD([sQuery(id+"F0.wireOp",EDGE,"E0")])],"isStart":false});
            var Q6;
            Q6=makeQuery(id+"F2.opExtrude","CAP_EDGE",EDGE,{"disambiguationData":[OSD([sQuery(id+"F0.wireOp",EDGE,"E1")])],"isStart":false});
            var Q7;
            Q7=makeQuery(id+"F2.opExtrude","CAP_EDGE",EDGE,{"disambiguationData":[OSD([sQuery(id+"F0.wireOp",EDGE,"E2")])],"isStart":false});
            var Q8;
            Q8=makeQuery(id+"F2.opExtrude","CAP_EDGE",EDGE,{"disambiguationData":[OSD([sQuery(id+"F0.wireOp",EDGE,"E3")])],"isStart":false});
            chamfer(context, id + "F7", {"entities" : qUnion([Q0, Q1, Q2, Q3, Q4, Q5, Q6, Q7, Q8]), "chamferType" : ChamferType.OFFSET_ANGLE, "width" : 0.15 * mm, "oppositeDirection" : false, "angle" : 60 * degree, "tangentPropagation" : true});
        }
        {
            var Q0;
            Q0=makeQuery(id+"F3.opExtrude","CAP_EDGE",EDGE,{"disambiguationData":[OSD([sQuery(id+"F0.wireOp",EDGE,"E60")])],"isStart":false});
            var Q1;
            Q1=makeQuery(id+"F3.opExtrude","CAP_EDGE",EDGE,{"disambiguationData":[OSD([sQuery(id+"F0.wireOp",EDGE,"E15")])],"isStart":false});
            var Q2;
            Q2=makeQuery(id+"F3.opExtrude","CAP_EDGE",EDGE,{"disambiguationData":[OSD([sQuery(id+"F0.wireOp",EDGE,"E40")])],"isStart":false});
            var Q3;
            Q3=makeQuery(id+"F3.opExtrude","CAP_EDGE",EDGE,{"disambiguationData":[OSD([sQuery(id+"F0.wireOp",EDGE,"E9")])],"isStart":false});
            var Q4;
            Q4=makeQuery(id+"F3.opExtrude","CAP_EDGE",EDGE,{"disambiguationData":[OSD([sQuery(id+"F0.wireOp",EDGE,"E41")])],"isStart":false});
            var Q5;
            Q5=makeQuery(id+"F3.opExtrude","CAP_EDGE",EDGE,{"disambiguationData":[OSD([sQuery(id+"F0.wireOp",EDGE,"E8")])],"isStart":false});
            var Q6;
            Q6=makeQuery(id+"F3.opExtrude","CAP_EDGE",EDGE,{"disambiguationData":[OSD([sQuery(id+"F0.wireOp",EDGE,"E10")])],"isStart":false});
            var Q7;
            Q7=makeQuery(id+"F3.opExtrude","CAP_EDGE",EDGE,{"disambiguationData":[OSD([sQuery(id+"F0.wireOp",EDGE,"E11")])],"isStart":false});
            var Q8;
            Q8=makeQuery(id+"F3.opExtrude","CAP_EDGE",EDGE,{"disambiguationData":[OSD([sQuery(id+"F0.wireOp",EDGE,"E42")])],"isStart":false});
            var Q9;
            Q9=makeQuery(id+"F3.opExtrude","CAP_EDGE",EDGE,{"disambiguationData":[OSD([sQuery(id+"F0.wireOp",EDGE,"E13")])],"isStart":false});
            var Q10;
            Q10=makeQuery(id+"F3.opExtrude","CAP_EDGE",EDGE,{"disambiguationData":[OSD([sQuery(id+"F0.wireOp",EDGE,"E12")])],"isStart":false});
            var Q11;
            Q11=makeQuery(id+"F3.opExtrude","CAP_EDGE",EDGE,{"disambiguationData":[OSD([sQuery(id+"F0.wireOp",EDGE,"E43")])],"isStart":false});
            var Q12;
            Q12=makeQuery(id+"F3.opExtrude","CAP_EDGE",EDGE,{"disambiguationData":[OSD([sQuery(id+"F0.wireOp",EDGE,"E14")])],"isStart":false});
            var Q13;
            Q13=makeQuery(id+"F1.opExtrude","CAP_EDGE",EDGE,{"disambiguationData":[OSD([sQuery(id+"F0.wireOp",EDGE,"E51")])],"isStart":false});
            var Q14;
            Q14=makeQuery(id+"F1.opExtrude","CAP_EDGE",EDGE,{"disambiguationData":[OSD([sQuery(id+"F0.wireOp",EDGE,"E50")])],"isStart":false});
            var Q15;
            Q15=makeQuery(id+"F1.opExtrude","CAP_EDGE",EDGE,{"disambiguationData":[OSD([sQuery(id+"F0.wireOp",EDGE,"E49")])],"isStart":false});
            var Q16;
            Q16=makeQuery(id+"F1.opExtrude","CAP_EDGE",EDGE,{"disambiguationData":[OSD([sQuery(id+"F0.wireOp",EDGE,"E48")])],"isStart":false});
            var Q17;
            Q17=makeQuery(id+"F1.opExtrude","CAP_EDGE",EDGE,{"disambiguationData":[OSD([sQuery(id+"F0.wireOp",EDGE,"E47")])],"isStart":false});
            var Q18;
            Q18=makeQuery(id+"F1.opExtrude","CAP_EDGE",EDGE,{"disambiguationData":[OSD([sQuery(id+"F0.wireOp",EDGE,"E45")])],"isStart":false});
            var Q19;
            Q19=makeQuery(id+"F1.opExtrude","CAP_EDGE",EDGE,{"disambiguationData":[OSD([sQuery(id+"F0.wireOp",EDGE,"E46")])],"isStart":false});
            var Q20;
            Q20=makeQuery(id+"F1.opExtrude","CAP_EDGE",EDGE,{"disambiguationData":[OSD([sQuery(id+"F0.wireOp",EDGE,"E44")])],"isStart":false});
            var Q21;
            Q21=makeQuery(id+"F1.opExtrude","CAP_EDGE",EDGE,{"disambiguationData":[OSD([sQuery(id+"F0.wireOp",EDGE,"E52")])],"isStart":false});
            var Q22;
            Q22=makeQuery(id+"F1.opExtrude","CAP_EDGE",EDGE,{"disambiguationData":[OSD([sQuery(id+"F0.wireOp",EDGE,"E55")])],"isStart":false});
            var Q23;
            Q23=makeQuery(id+"F1.opExtrude","CAP_EDGE",EDGE,{"disambiguationData":[OSD([sQuery(id+"F0.wireOp",EDGE,"E53")])],"isStart":false});
            var Q24;
            Q24=makeQuery(id+"F1.opExtrude","CAP_EDGE",EDGE,{"disambiguationData":[OSD([sQuery(id+"F0.wireOp",EDGE,"E54")])],"isStart":false});
            var Q25;
            Q25=makeQuery(id+"F1.opExtrude","CAP_EDGE",EDGE,{"disambiguationData":[OSD([sQuery(id+"F0.wireOp",EDGE,"E56")])],"isStart":false});
            var Q26;
            Q26=makeQuery(id+"F1.opExtrude","CAP_EDGE",EDGE,{"disambiguationData":[OSD([sQuery(id+"F0.wireOp",EDGE,"E58")])],"isStart":false});
            var Q27;
            Q27=makeQuery(id+"F1.opExtrude","CAP_EDGE",EDGE,{"disambiguationData":[OSD([sQuery(id+"F0.wireOp",EDGE,"E57")])],"isStart":false});
            var Q28;
            Q28=makeQuery(id+"F1.opExtrude","CAP_EDGE",EDGE,{"disambiguationData":[OSD([sQuery(id+"F0.wireOp",EDGE,"E59")])],"isStart":false});
            chamfer(context, id + "F8", {"entities" : qUnion([Q0, Q1, Q2, Q3, Q4, Q5, Q6, Q7, Q8, Q9, Q10, Q11, Q12, Q13, Q14, Q15, Q16, Q17, Q18, Q19, Q20, Q21, Q22, Q23, Q24, Q25, Q26, Q27, Q28]), "width" : 0.5 * mm, "tangentPropagation" : true});
        }
        {
            var Q0;
            Q0=makeQuery(id+"F1.opExtrude","CAP_EDGE",EDGE,{"disambiguationData":[OSD([sQuery(id+"F0.wireOp",EDGE,"E36")])],"isStart":false});
            var Q1;
            Q1=makeQuery(id+"F1.opExtrude","CAP_EDGE",EDGE,{"disambiguationData":[OSD([sQuery(id+"F0.wireOp",EDGE,"E37")])],"isStart":false});
            var Q2;
            Q2=makeQuery(id+"F1.opExtrude","CAP_EDGE",EDGE,{"disambiguationData":[OSD([sQuery(id+"F0.wireOp",EDGE,"E38")])],"isStart":false});
            var Q3;
            {var subQ0=sQuery(id+"F0.wireOp",EDGE,"E32");Q3=makeQuery(id+"F1.opExtrude","CAP_EDGE",EDGE,{"disambiguationData":[OSD([subQ0]),TDD([makeQuery(id+"F0.imprint","IMPRINT",EDGE,{"disambiguationData":[TD([[makeQuery(id+"F0.imprint","INTERSECT",VERTEX,{"derivedFrom":[subQ0,sQuery(id+"F0.wireOp",EDGE,"E33")]}),1.0]])],"derivedFrom":subQ0})])],"isStart":false});}
            var Q4;
            Q4=makeQuery(id+"F1.opExtrude","CAP_EDGE",EDGE,{"disambiguationData":[OSD([sQuery(id+"F0.wireOp",EDGE,"E39")])],"isStart":false});
            var Q5;
            {var subQ0=sQuery(id+"F0.wireOp",EDGE,"E32");Q5=makeQuery(id+"F1.opExtrude","CAP_EDGE",EDGE,{"disambiguationData":[OSD([subQ0]),TDD([makeQuery(id+"F0.imprint","IMPRINT",EDGE,{"disambiguationData":[TD([[makeQuery(id+"F0.imprint","INTERSECT",VERTEX,{"derivedFrom":[sQuery(id+"F0.wireOp",EDGE,"E31"),subQ0]}),-1.0]])],"derivedFrom":subQ0})])],"isStart":false});}
            var Q6;
            {var subQ0=sQuery(id+"F0.wireOp",EDGE,"E26");Q6=makeQuery(id+"F1.opExtrude","CAP_EDGE",EDGE,{"disambiguationData":[OSD([subQ0]),TDD([makeQuery(id+"F0.imprint","IMPRINT",EDGE,{"disambiguationData":[TD([[makeQuery(id+"F0.imprint","INTERSECT",VERTEX,{"derivedFrom":[sQuery(id+"F0.wireOp",EDGE,"E25"),subQ0]}),-1.0]])],"derivedFrom":subQ0})])],"isStart":false});}
            var Q7;
            {var subQ0=sQuery(id+"F0.wireOp",EDGE,"E26");Q7=makeQuery(id+"F1.opExtrude","CAP_EDGE",EDGE,{"disambiguationData":[OSD([subQ0]),TDD([makeQuery(id+"F0.imprint","IMPRINT",EDGE,{"disambiguationData":[TD([[makeQuery(id+"F0.imprint","INTERSECT",VERTEX,{"derivedFrom":[subQ0,sQuery(id+"F0.wireOp",EDGE,"E27")]}),1.0]])],"derivedFrom":subQ0})])],"isStart":false});}
            fillet(context, id + "F9", {"entities" : qUnion([Q0, Q1, Q2, Q3, Q4, Q5, Q6, Q7]), "radius" : 0.2 * mm, "tangentPropagation" : true, "allowEdgeOverflow" : false});
        }
    });
